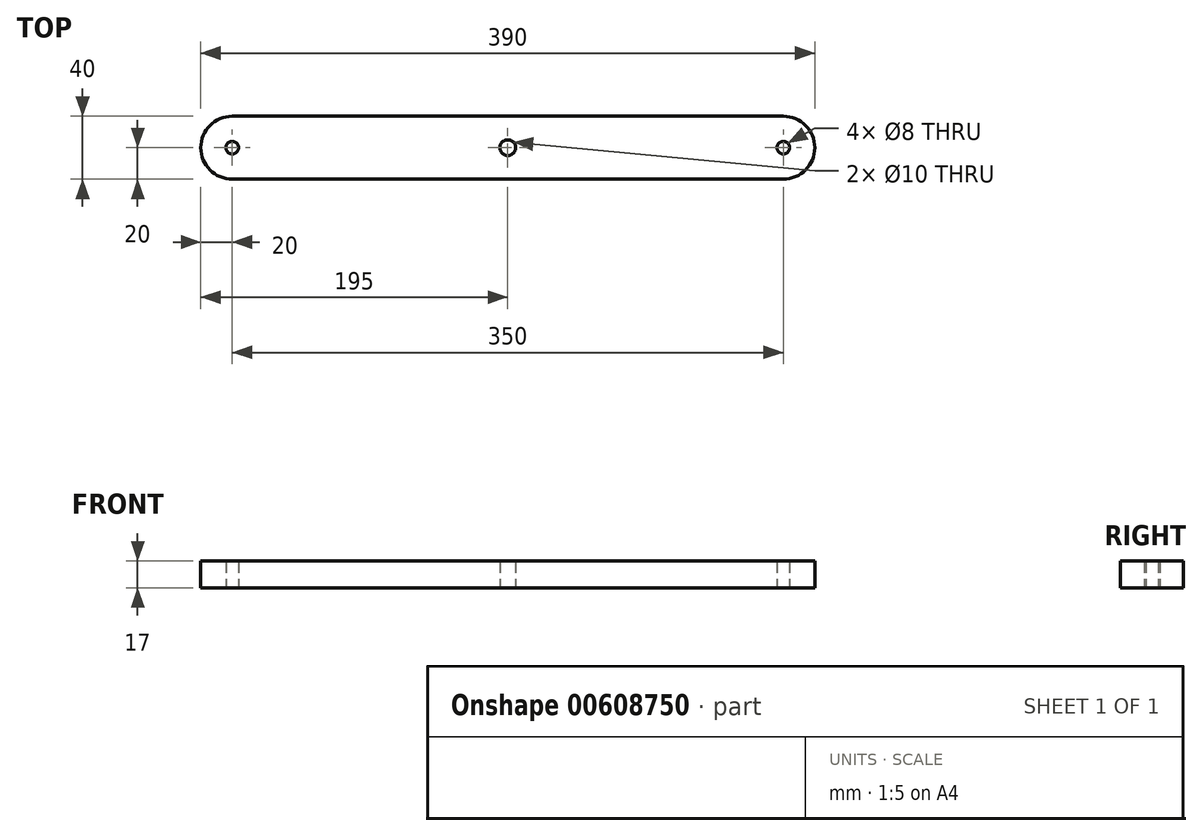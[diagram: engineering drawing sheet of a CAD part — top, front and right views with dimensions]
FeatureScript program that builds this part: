
annotation { "Feature Type Name" : "Feature", "Feature Type Description" : "" }
export const myFeature = defineFeature(function(context is Context, id is Id, definition is map)
    precondition{}
    {
        {
            var Q0;
            Q0=qCreatedBy(makeId("Top.planeOp"),FACE);
            var sketch = newSketch(context, id + "F0", { "sketchPlane" : qUnion([Q0])});
            skLineSegment(sketch, "E0.bottom", {"start": v(175, 20.13) * mm, "end": v(-175, 20.13) * mm});
            skLineSegment(sketch, "E0.top", {"start": v(175, -19.87) * mm, "end": v(-175, -19.87) * mm});
            skPoint(sketch, "E0.middle", {"position": v(0, 0.13) * mm});
            skCircle(sketch, "E1", {"center": v(-175, 0.13) * mm, "radius": 4 * mm});
            skCircle(sketch, "E2", {"center": v(175, 0.13) * mm, "radius": 4 * mm});
            skCircle(sketch, "E3", {"center": v(0, 0.13) * mm, "radius": 5 * mm});
            skArc(sketch, "E4", {"start": v(-175, 20.13) * mm, "mid": v(-195, 0.13) * mm, "end": v(-175, -19.87) * mm});
            skLineSegment(sketch, "E5", {"start": v(-175, 47.4) * mm, "end": v(-175, -53.22) * mm, "construction": true});
            skLineSegment(sketch, "E6", {"start": v(175, 56.38) * mm, "end": v(175, -52.62) * mm, "construction": true});
            skArc(sketch, "E7", {"start": v(175, -19.87) * mm, "mid": v(195, 0.13) * mm, "end": v(175, 20.13) * mm});
            skSolve(sketch);
        }
        {
            var Q0;
            Q0=makeQuery(id+"F0.imprint","IMPRINT",FACE,{"disambiguationData":[TD([[makeQuery(id+"F0.imprint","IMPRINT",EDGE,{"derivedFrom":sQuery(id+"F0.wireOp",EDGE,"E0.bottom")}),1.0]])]});
            extrude(context, id + "F1", {"entities" : qUnion([Q0]), "depth" : 17 * mm, "offsetDistance" : 25 * mm});
        }
    });
